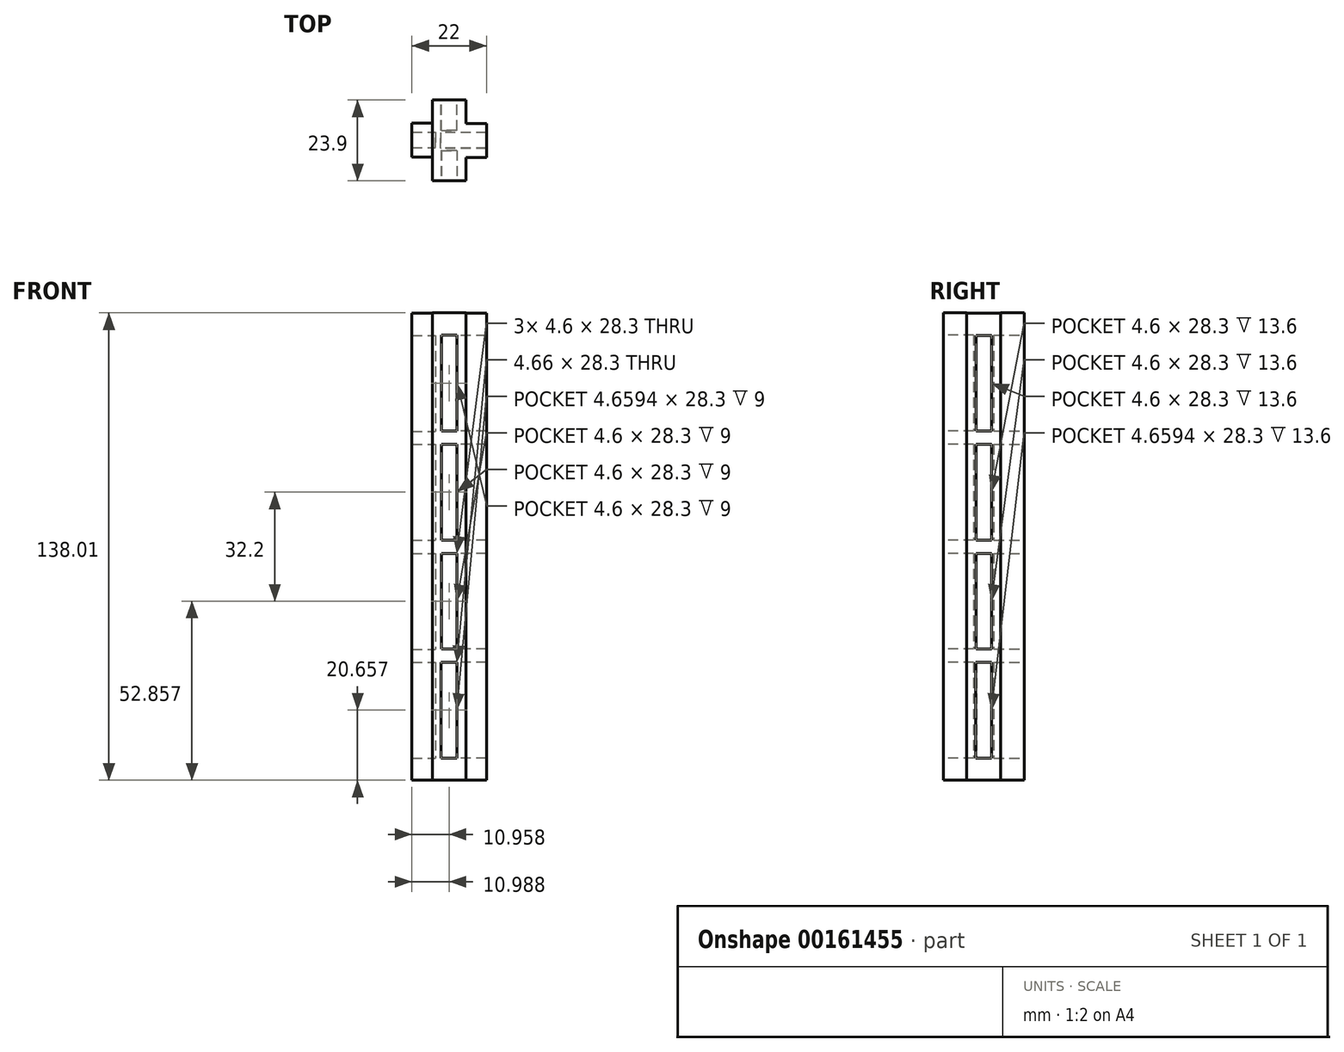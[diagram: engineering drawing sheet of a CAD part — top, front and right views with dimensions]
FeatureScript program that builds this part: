
annotation { "Feature Type Name" : "Feature", "Feature Type Description" : "" }
export const myFeature = defineFeature(function(context is Context, id is Id, definition is map)
    precondition{}
    {
        {
            var Q0;
            Q0=qCreatedBy(makeId("Front.planeOp"),FACE);
            var sketch = newSketch(context, id + "F0", { "sketchPlane" : qUnion([Q0])});
            skLineSegment(sketch, "E0.bottom", {"start": v(-30.25, 56.68) * mm, "end": v(-20.25, 56.68) * mm});
            skLineSegment(sketch, "E0.top", {"start": v(-30.25, -81.32) * mm, "end": v(-20.25, -81.32) * mm});
            skLineSegment(sketch, "E0.left", {"start": v(-30.25, 56.68) * mm, "end": v(-30.25, -81.32) * mm});
            skLineSegment(sketch, "E0.right", {"start": v(-20.25, 56.68) * mm, "end": v(-20.25, -81.32) * mm});
            skLineSegment(sketch, "E1.bottom", {"start": v(-27.56, 50.08) * mm, "end": v(-22.96, 50.08) * mm});
            skLineSegment(sketch, "E1.top", {"start": v(-27.56, 21.78) * mm, "end": v(-22.96, 21.78) * mm});
            skLineSegment(sketch, "E1.left", {"start": v(-27.56, 50.08) * mm, "end": v(-27.56, 21.78) * mm});
            skLineSegment(sketch, "E1.right", {"start": v(-22.96, 50.08) * mm, "end": v(-22.96, 21.78) * mm});
            skLineSegment(sketch, "E2", {"start": v(-26.53, 56.68) * mm, "end": v(-26.53, 50.08) * mm, "construction": true});
            skLineSegment(sketch, "E3", {"start": v(-27.56, 45.9) * mm, "end": v(-30.25, 45.9) * mm, "construction": true});
            skLineSegment(sketch, "E4", {"start": v(-22.96, 46.31) * mm, "end": v(-20.25, 46.31) * mm, "construction": true});
            skLineSegment(sketch, "E5", {"start": v(-25.26, 21.78) * mm, "end": v(-25.26, 17.88) * mm, "construction": true});
            skLineSegment(sketch, "E6", {"start": v(-27.56, 21.78) * mm, "end": v(-27.56, 17.88) * mm, "construction": true});
            skLineSegment(sketch, "E7", {"start": v(-22.96, 21.78) * mm, "end": v(-22.96, 17.88) * mm, "construction": true});
            skLineSegment(sketch, "E8.bottom", {"start": v(-27.56, 17.88) * mm, "end": v(-22.96, 17.88) * mm});
            skLineSegment(sketch, "E8.top", {"start": v(-27.56, -10.42) * mm, "end": v(-22.96, -10.42) * mm});
            skLineSegment(sketch, "E8.left", {"start": v(-27.56, 17.88) * mm, "end": v(-27.56, -10.42) * mm});
            skLineSegment(sketch, "E8.right", {"start": v(-22.96, 17.88) * mm, "end": v(-22.96, -10.42) * mm});
            skLineSegment(sketch, "E9", {"start": v(-22.96, -10.42) * mm, "end": v(-22.96, -14.32) * mm, "construction": true});
            skLineSegment(sketch, "E10", {"start": v(-27.56, -10.42) * mm, "end": v(-27.56, -14.32) * mm, "construction": true});
            skLineSegment(sketch, "E11.bottom", {"start": v(-27.56, -14.32) * mm, "end": v(-22.96, -14.32) * mm});
            skLineSegment(sketch, "E11.top", {"start": v(-27.56, -42.62) * mm, "end": v(-22.96, -42.62) * mm});
            skLineSegment(sketch, "E11.left", {"start": v(-27.56, -14.32) * mm, "end": v(-27.56, -42.62) * mm});
            skLineSegment(sketch, "E11.right", {"start": v(-22.96, -14.32) * mm, "end": v(-22.96, -42.62) * mm});
            skLineSegment(sketch, "E12", {"start": v(-27.56, -41.18) * mm, "end": v(-27.56, -42.62) * mm});
            skLineSegment(sketch, "E13", {"start": v(-22.96, -42.62) * mm, "end": v(-22.96, -46.52) * mm, "construction": true});
            skLineSegment(sketch, "E14.bottom", {"start": v(-22.96, -46.52) * mm, "end": v(-27.62, -46.52) * mm});
            skLineSegment(sketch, "E14.top", {"start": v(-22.96, -74.82) * mm, "end": v(-27.62, -74.82) * mm});
            skLineSegment(sketch, "E14.left", {"start": v(-22.96, -46.52) * mm, "end": v(-22.96, -74.82) * mm});
            skLineSegment(sketch, "E14.right", {"start": v(-27.62, -46.52) * mm, "end": v(-27.62, -74.82) * mm});
            skLineSegment(sketch, "E15", {"start": v(-22.96, -74.82) * mm, "end": v(-22.96, -81.32) * mm, "construction": true});
            skSolve(sketch);
        }
        {
            var Q0;
            Q0=makeQuery(id+"F0.imprint","IMPRINT",FACE,{"disambiguationData":[TD([[makeQuery(id+"F0.imprint","IMPRINT",EDGE,{"derivedFrom":sQuery(id+"F0.wireOp",EDGE,"E0.bottom")}),-1.0]])]});
            var Q1;
            Q1=makeQuery(id+"F0.imprint","IMPRINT",FACE,{"disambiguationData":[TD([[makeQuery(id+"F0.imprint","IMPRINT",EDGE,{"derivedFrom":sQuery(id+"F0.wireOp",EDGE,"E1.bottom")}),-1.0]])]});
            var Q2;
            Q2=makeQuery(id+"F0.imprint","IMPRINT",FACE,{"disambiguationData":[TD([[makeQuery(id+"F0.imprint","IMPRINT",EDGE,{"derivedFrom":sQuery(id+"F0.wireOp",EDGE,"E8.bottom")}),-1.0]])]});
            var Q3;
            Q3=makeQuery(id+"F0.imprint","IMPRINT",FACE,{"disambiguationData":[TD([[makeQuery(id+"F0.imprint","IMPRINT",EDGE,{"derivedFrom":sQuery(id+"F0.wireOp",EDGE,"E11.bottom")}),-1.0]])]});
            var Q4;
            Q4=makeQuery(id+"F0.imprint","IMPRINT",FACE,{"disambiguationData":[TD([[makeQuery(id+"F0.imprint","IMPRINT",EDGE,{"derivedFrom":sQuery(id+"F0.wireOp",EDGE,"E14.bottom")}),1.0]])]});
            extrude(context, id + "F1", {"entities" : qUnion([Q0, Q1, Q2, Q3, Q4]), "depth" : 11.95 * mm});
        }
        {
            var Q0;
            Q0=makeQuery(id+"F0.imprint","IMPRINT",FACE,{"disambiguationData":[TD([[makeQuery(id+"F0.imprint","IMPRINT",EDGE,{"derivedFrom":sQuery(id+"F0.wireOp",EDGE,"E1.bottom")}),-1.0]])]});
            var Q1;
            Q1=makeQuery(id+"F0.imprint","IMPRINT",FACE,{"disambiguationData":[TD([[makeQuery(id+"F0.imprint","IMPRINT",EDGE,{"derivedFrom":sQuery(id+"F0.wireOp",EDGE,"E8.bottom")}),-1.0]])]});
            var Q2;
            Q2=makeQuery(id+"F0.imprint","IMPRINT",FACE,{"disambiguationData":[TD([[makeQuery(id+"F0.imprint","IMPRINT",EDGE,{"derivedFrom":sQuery(id+"F0.wireOp",EDGE,"E11.bottom")}),-1.0]])]});
            var Q3;
            Q3=makeQuery(id+"F0.imprint","IMPRINT",FACE,{"disambiguationData":[TD([[makeQuery(id+"F0.imprint","IMPRINT",EDGE,{"derivedFrom":sQuery(id+"F0.wireOp",EDGE,"E14.bottom")}),1.0]])]});
            extrude(context, id + "F2", {"entities" : qUnion([Q0, Q1, Q2, Q3]), "operationType" : NewBodyOperationType.REMOVE, "depth" : 9 * mm});
        }
        {
            var Q0;
            Q0=makeQuery(id+"F1.opExtrude","SWEPT_BODY",BODY,{"disambiguationData":[OSD([sQuery(id+"F0.wireOp",EDGE,"E0.bottom"),sQuery(id+"F0.wireOp",EDGE,"E0.top"),sQuery(id+"F0.wireOp",EDGE,"E0.left"),sQuery(id+"F0.wireOp",EDGE,"E0.right")])]});
            var Q1;
            Q1=makeQuery(id+"F1.opExtrude","CAP_FACE",FACE,{"disambiguationData":[OSD([sQuery(id+"F0.wireOp",EDGE,"E0.bottom"),sQuery(id+"F0.wireOp",EDGE,"E0.top"),sQuery(id+"F0.wireOp",EDGE,"E0.left"),sQuery(id+"F0.wireOp",EDGE,"E0.right")])],"isStart":false});
            mirror(context, id + "F3", {"operationType" : NewBodyOperationType.ADD, "entities" : qUnion([Q0]), "mirrorPlane" : qUnion([Q1])});
        }
        {
            var Q0;
            {var subQ0=makeQuery(id+"F1.opExtrude","SWEPT_FACE",FACE,{"disambiguationData":[OSD([sQuery(id+"F0.wireOp",EDGE,"E0.right")])]});Q0=makeQuery(id+"F3.boolean.opBoolean","MERGE",FACE,{"derivedFrom":[subQ0,makeQuery(id+"F3.opPattern","COPY",FACE,{"derivedFrom":subQ0,"instanceName":"1"})]});}
            var sketch = newSketch(context, id + "F4", { "sketchPlane" : qUnion([Q0])});
            skLineSegment(sketch, "E16.bottom", {"start": v(-16.93, 56.67) * mm, "end": v(-6.93, 56.67) * mm});
            skLineSegment(sketch, "E16.top", {"start": v(-16.93, -81.33) * mm, "end": v(-6.93, -81.33) * mm});
            skLineSegment(sketch, "E16.left", {"start": v(-16.93, 56.67) * mm, "end": v(-16.93, -81.33) * mm});
            skLineSegment(sketch, "E16.right", {"start": v(-6.93, 56.67) * mm, "end": v(-6.93, -81.33) * mm});
            skLineSegment(sketch, "E17.bottom", {"start": v(-14.24, 50.07) * mm, "end": v(-9.64, 50.07) * mm});
            skLineSegment(sketch, "E17.top", {"start": v(-14.24, 21.77) * mm, "end": v(-9.64, 21.77) * mm});
            skLineSegment(sketch, "E17.left", {"start": v(-14.24, 50.07) * mm, "end": v(-14.24, 21.77) * mm});
            skLineSegment(sketch, "E17.right", {"start": v(-9.64, 50.07) * mm, "end": v(-9.64, 21.77) * mm});
            skLineSegment(sketch, "E18", {"start": v(-13.2, 56.67) * mm, "end": v(-13.2, 50.07) * mm, "construction": true});
            skLineSegment(sketch, "E19", {"start": v(-14.24, 45.9) * mm, "end": v(-16.93, 45.9) * mm, "construction": true});
            skLineSegment(sketch, "E20", {"start": v(-9.64, 46.3) * mm, "end": v(-6.93, 46.3) * mm, "construction": true});
            skLineSegment(sketch, "E21", {"start": v(-11.94, 21.77) * mm, "end": v(-11.94, 17.87) * mm, "construction": true});
            skLineSegment(sketch, "E22", {"start": v(-14.24, 21.77) * mm, "end": v(-14.24, 17.87) * mm, "construction": true});
            skLineSegment(sketch, "E23", {"start": v(-9.64, 21.77) * mm, "end": v(-9.64, 17.87) * mm, "construction": true});
            skLineSegment(sketch, "E24.bottom", {"start": v(-14.24, 17.87) * mm, "end": v(-9.64, 17.87) * mm});
            skLineSegment(sketch, "E24.top", {"start": v(-14.24, -10.43) * mm, "end": v(-9.64, -10.43) * mm});
            skLineSegment(sketch, "E24.left", {"start": v(-14.24, 17.87) * mm, "end": v(-14.24, -10.43) * mm});
            skLineSegment(sketch, "E24.right", {"start": v(-9.64, 17.87) * mm, "end": v(-9.64, -10.43) * mm});
            skLineSegment(sketch, "E25", {"start": v(-9.64, -10.43) * mm, "end": v(-9.64, -14.33) * mm, "construction": true});
            skLineSegment(sketch, "E26", {"start": v(-14.24, -10.43) * mm, "end": v(-14.24, -14.33) * mm, "construction": true});
            skLineSegment(sketch, "E27.bottom", {"start": v(-14.24, -14.33) * mm, "end": v(-9.64, -14.33) * mm});
            skLineSegment(sketch, "E27.top", {"start": v(-14.24, -42.63) * mm, "end": v(-9.64, -42.63) * mm});
            skLineSegment(sketch, "E27.left", {"start": v(-14.24, -14.33) * mm, "end": v(-14.24, -42.63) * mm});
            skLineSegment(sketch, "E27.right", {"start": v(-9.64, -14.33) * mm, "end": v(-9.64, -42.63) * mm});
            skLineSegment(sketch, "E28", {"start": v(-14.24, 18.57) * mm, "end": v(-14.24, -42.63) * mm});
            skLineSegment(sketch, "E29", {"start": v(-9.64, -42.63) * mm, "end": v(-9.64, -46.53) * mm, "construction": true});
            skLineSegment(sketch, "E30.bottom", {"start": v(-9.64, -46.53) * mm, "end": v(-14.3, -46.53) * mm});
            skLineSegment(sketch, "E30.top", {"start": v(-9.64, -74.83) * mm, "end": v(-14.3, -74.83) * mm});
            skLineSegment(sketch, "E30.left", {"start": v(-9.64, -46.53) * mm, "end": v(-9.64, -74.83) * mm});
            skLineSegment(sketch, "E30.right", {"start": v(-14.3, -46.53) * mm, "end": v(-14.3, -74.83) * mm});
            skLineSegment(sketch, "E31", {"start": v(-9.64, -74.83) * mm, "end": v(-9.64, -81.33) * mm, "construction": true});
            skSolve(sketch);
        }
        {
            var Q0;
            Q0=qSketchRegion(id+"F4",true);
            extrude(context, id + "F5", {"entities" : qUnion([Q0]), "operationType" : NewBodyOperationType.ADD, "depth" : 6 * mm});
        }
        {
            var Q0;
            {var subQ0=makeQuery(id+"F1.opExtrude","SWEPT_FACE",FACE,{"disambiguationData":[OSD([sQuery(id+"F0.wireOp",EDGE,"E0.right")])]});Q0=makeQuery(id+"F5.boolean.opBoolean","SPLIT",FACE,{"disambiguationData":[TD([makeQuery(id+"F5.opExtrude","SWEPT_FACE",FACE,{"disambiguationData":[OSD([sQuery(id+"F4.wireOp",EDGE,"E17.bottom")])]})])],"derivedFrom":makeQuery(id+"F3.boolean.opBoolean","MERGE",FACE,{"derivedFrom":[subQ0,makeQuery(id+"F3.opPattern","COPY",FACE,{"derivedFrom":subQ0,"instanceName":"1"})]})});}
            var Q1;
            {var subQ0=sQuery(id+"F4.wireOp",EDGE,"E24.bottom");var subQ3=makeQuery(id+"F1.opExtrude","SWEPT_FACE",FACE,{"disambiguationData":[OSD([sQuery(id+"F0.wireOp",EDGE,"E0.right")])]});Q1=makeQuery(id+"F5.boolean.opBoolean","SPLIT",FACE,{"disambiguationData":[TD([makeQuery(id+"F5.opExtrude","SWEPT_FACE",FACE,{"disambiguationData":[OSD([subQ0])]})])],"derivedFrom":makeQuery(id+"F3.boolean.opBoolean","MERGE",FACE,{"derivedFrom":[subQ3,makeQuery(id+"F3.opPattern","COPY",FACE,{"derivedFrom":subQ3,"instanceName":"1"})]})});}
            var Q2;
            {var subQ0=sQuery(id+"F4.wireOp",EDGE,"E27.bottom");var subQ3=makeQuery(id+"F1.opExtrude","SWEPT_FACE",FACE,{"disambiguationData":[OSD([sQuery(id+"F0.wireOp",EDGE,"E0.right")])]});Q2=makeQuery(id+"F5.boolean.opBoolean","SPLIT",FACE,{"disambiguationData":[TD([makeQuery(id+"F5.opExtrude","SWEPT_FACE",FACE,{"disambiguationData":[OSD([subQ0])]})])],"derivedFrom":makeQuery(id+"F3.boolean.opBoolean","MERGE",FACE,{"derivedFrom":[subQ3,makeQuery(id+"F3.opPattern","COPY",FACE,{"derivedFrom":subQ3,"instanceName":"1"})]})});}
            var Q3;
            {var subQ0=makeQuery(id+"F1.opExtrude","SWEPT_FACE",FACE,{"disambiguationData":[OSD([sQuery(id+"F0.wireOp",EDGE,"E0.right")])]});Q3=makeQuery(id+"F5.boolean.opBoolean","SPLIT",FACE,{"disambiguationData":[TD([makeQuery(id+"F5.opExtrude","SWEPT_FACE",FACE,{"disambiguationData":[OSD([sQuery(id+"F4.wireOp",EDGE,"E30.bottom")])]})])],"derivedFrom":makeQuery(id+"F3.boolean.opBoolean","MERGE",FACE,{"derivedFrom":[subQ0,makeQuery(id+"F3.opPattern","COPY",FACE,{"derivedFrom":subQ0,"instanceName":"1"})]})});}
            extrude(context, id + "F6", {"entities" : qUnion([Q0, Q1, Q2, Q3]), "operationType" : NewBodyOperationType.REMOVE, "oppositeDirection" : true, "depth" : 7.6 * mm});
        }
        {
            var Q0;
            {var subQ0=makeQuery(id+"F1.opExtrude","SWEPT_FACE",FACE,{"disambiguationData":[OSD([sQuery(id+"F0.wireOp",EDGE,"E0.left")])]});Q0=makeQuery(id+"F3.boolean.opBoolean","MERGE",FACE,{"derivedFrom":[subQ0,makeQuery(id+"F3.opPattern","COPY",FACE,{"derivedFrom":subQ0,"instanceName":"1"})]});}
            var sketch = newSketch(context, id + "F7", { "sketchPlane" : qUnion([Q0])});
            skLineSegment(sketch, "E32.bottom", {"start": v(6.83, 56.64) * mm, "end": v(16.83, 56.64) * mm});
            skLineSegment(sketch, "E32.top", {"start": v(6.83, -81.36) * mm, "end": v(16.83, -81.36) * mm});
            skLineSegment(sketch, "E32.left", {"start": v(6.83, 56.64) * mm, "end": v(6.83, -81.36) * mm});
            skLineSegment(sketch, "E32.right", {"start": v(16.83, 56.64) * mm, "end": v(16.83, -81.36) * mm});
            skLineSegment(sketch, "E33.bottom", {"start": v(9.52, 50.04) * mm, "end": v(14.12, 50.04) * mm});
            skLineSegment(sketch, "E33.top", {"start": v(9.52, 21.74) * mm, "end": v(14.12, 21.74) * mm});
            skLineSegment(sketch, "E33.left", {"start": v(9.52, 50.04) * mm, "end": v(9.52, 21.74) * mm});
            skLineSegment(sketch, "E33.right", {"start": v(14.12, 50.04) * mm, "end": v(14.12, 21.74) * mm});
            skLineSegment(sketch, "E34", {"start": v(10.56, 56.64) * mm, "end": v(10.56, 50.04) * mm, "construction": true});
            skLineSegment(sketch, "E35", {"start": v(9.52, 45.86) * mm, "end": v(6.83, 45.86) * mm, "construction": true});
            skLineSegment(sketch, "E36", {"start": v(14.12, 46.27) * mm, "end": v(16.83, 46.27) * mm, "construction": true});
            skLineSegment(sketch, "E37", {"start": v(11.82, 21.74) * mm, "end": v(11.82, 17.84) * mm, "construction": true});
            skLineSegment(sketch, "E38", {"start": v(9.52, 21.74) * mm, "end": v(9.52, 17.84) * mm, "construction": true});
            skLineSegment(sketch, "E39", {"start": v(14.12, 21.74) * mm, "end": v(14.12, 17.84) * mm, "construction": true});
            skLineSegment(sketch, "E40.bottom", {"start": v(9.52, 17.84) * mm, "end": v(14.12, 17.84) * mm});
            skLineSegment(sketch, "E40.top", {"start": v(9.52, -10.46) * mm, "end": v(14.12, -10.46) * mm});
            skLineSegment(sketch, "E40.left", {"start": v(9.52, 17.84) * mm, "end": v(9.52, -10.46) * mm});
            skLineSegment(sketch, "E40.right", {"start": v(14.12, 17.84) * mm, "end": v(14.12, -10.46) * mm});
            skLineSegment(sketch, "E41", {"start": v(14.12, -10.46) * mm, "end": v(14.12, -14.36) * mm, "construction": true});
            skLineSegment(sketch, "E42", {"start": v(9.52, -10.46) * mm, "end": v(9.52, -14.36) * mm, "construction": true});
            skLineSegment(sketch, "E43.bottom", {"start": v(9.52, -14.36) * mm, "end": v(14.12, -14.36) * mm});
            skLineSegment(sketch, "E43.top", {"start": v(9.52, -42.66) * mm, "end": v(14.12, -42.66) * mm});
            skLineSegment(sketch, "E43.left", {"start": v(9.52, -14.36) * mm, "end": v(9.52, -42.66) * mm});
            skLineSegment(sketch, "E43.right", {"start": v(14.12, -14.36) * mm, "end": v(14.12, -42.66) * mm});
            skLineSegment(sketch, "E44", {"start": v(9.52, -40.6) * mm, "end": v(9.52, -42.66) * mm});
            skLineSegment(sketch, "E45", {"start": v(14.12, -42.66) * mm, "end": v(14.12, -46.56) * mm, "construction": true});
            skLineSegment(sketch, "E46.bottom", {"start": v(14.12, -46.56) * mm, "end": v(9.46, -46.56) * mm});
            skLineSegment(sketch, "E46.top", {"start": v(14.12, -74.86) * mm, "end": v(9.46, -74.86) * mm});
            skLineSegment(sketch, "E46.left", {"start": v(14.12, -46.56) * mm, "end": v(14.12, -74.86) * mm});
            skLineSegment(sketch, "E46.right", {"start": v(9.46, -46.56) * mm, "end": v(9.46, -74.86) * mm});
            skLineSegment(sketch, "E47", {"start": v(14.12, -74.86) * mm, "end": v(14.12, -81.36) * mm, "construction": true});
            skSolve(sketch);
        }
        {
            var Q0;
            {var subQ0=sQuery(id+"F7.wireOp",EDGE,"E32.bottom");Q0=makeQuery(id+"F7.imprint","IMPRINT",FACE,{"disambiguationData":[TD([[makeQuery(id+"F7.imprint","IMPRINT",EDGE,{"derivedFrom":subQ0}),-1.0]])]});}
            var Q1;
            Q1=sQuery(id+"F7.wireOp",EDGE,"E32.bottom");
            var Q2;
            Q2=sQuery(id+"F7.wireOp",EDGE,"E32.top");
            var Q3;
            Q3=sQuery(id+"F7.wireOp",EDGE,"E32.left");
            var Q4;
            Q4=sQuery(id+"F7.wireOp",EDGE,"E32.right");
            var Q5;
            Q5=sQuery(id+"F7.wireOp",EDGE,"E33.bottom");
            var Q6;
            Q6=sQuery(id+"F7.wireOp",EDGE,"E33.top");
            var Q7;
            Q7=sQuery(id+"F7.wireOp",EDGE,"E33.left");
            var Q8;
            Q8=sQuery(id+"F7.wireOp",EDGE,"E33.right");
            var Q9;
            Q9=sQuery(id+"F7.wireOp",EDGE,"E40.bottom");
            var Q10;
            Q10=sQuery(id+"F7.wireOp",EDGE,"E40.top");
            var Q11;
            Q11=sQuery(id+"F7.wireOp",EDGE,"E40.left");
            var Q12;
            Q12=sQuery(id+"F7.wireOp",EDGE,"E40.right");
            var Q13;
            Q13=sQuery(id+"F7.wireOp",EDGE,"E43.bottom");
            var Q14;
            Q14=sQuery(id+"F7.wireOp",EDGE,"E43.top");
            var Q15;
            Q15=sQuery(id+"F7.wireOp",EDGE,"E43.left");
            var Q16;
            Q16=sQuery(id+"F7.wireOp",EDGE,"E43.right");
            var Q17;
            Q17=sQuery(id+"F7.wireOp",EDGE,"E44");
            var Q18;
            Q18=sQuery(id+"F7.wireOp",EDGE,"E46.bottom");
            var Q19;
            Q19=sQuery(id+"F7.wireOp",EDGE,"E46.top");
            var Q20;
            Q20=sQuery(id+"F7.wireOp",EDGE,"E46.left");
            var Q21;
            Q21=sQuery(id+"F7.wireOp",EDGE,"E46.right");
            extrude(context, id + "F8", {"entities" : qUnion([Q0]), "operationType" : NewBodyOperationType.ADD, "surfaceEntities" : qUnion([Q1, Q2, Q3, Q4, Q5, Q6, Q7, Q8, Q9, Q10, Q11, Q12, Q13, Q14, Q15, Q16, Q17, Q18, Q19, Q20, Q21]), "depth" : 6 * mm});
        }
        {
            var Q0;
            {var subQ0=makeQuery(id+"F1.opExtrude","SWEPT_FACE",FACE,{"disambiguationData":[OSD([sQuery(id+"F0.wireOp",EDGE,"E0.left")])]});Q0=makeQuery(id+"F8.boolean.opBoolean","SPLIT",FACE,{"disambiguationData":[TD([makeQuery(id+"F8.opExtrude","SWEPT_FACE",FACE,{"disambiguationData":[OSD([sQuery(id+"F7.wireOp",EDGE,"E33.bottom")])]})])],"derivedFrom":makeQuery(id+"F3.boolean.opBoolean","MERGE",FACE,{"derivedFrom":[subQ0,makeQuery(id+"F3.opPattern","COPY",FACE,{"derivedFrom":subQ0,"instanceName":"1"})]})});}
            var Q1;
            {var subQ0=makeQuery(id+"F1.opExtrude","SWEPT_FACE",FACE,{"disambiguationData":[OSD([sQuery(id+"F0.wireOp",EDGE,"E0.left")])]});Q1=makeQuery(id+"F8.boolean.opBoolean","SPLIT",FACE,{"disambiguationData":[TD([makeQuery(id+"F8.opExtrude","SWEPT_FACE",FACE,{"disambiguationData":[OSD([sQuery(id+"F7.wireOp",EDGE,"E40.bottom")])]})])],"derivedFrom":makeQuery(id+"F3.boolean.opBoolean","MERGE",FACE,{"derivedFrom":[subQ0,makeQuery(id+"F3.opPattern","COPY",FACE,{"derivedFrom":subQ0,"instanceName":"1"})]})});}
            var Q2;
            {var subQ0=makeQuery(id+"F1.opExtrude","SWEPT_FACE",FACE,{"disambiguationData":[OSD([sQuery(id+"F0.wireOp",EDGE,"E0.left")])]});Q2=makeQuery(id+"F8.boolean.opBoolean","SPLIT",FACE,{"disambiguationData":[TD([makeQuery(id+"F8.opExtrude","SWEPT_FACE",FACE,{"disambiguationData":[OSD([sQuery(id+"F7.wireOp",EDGE,"E46.bottom")])]})])],"derivedFrom":makeQuery(id+"F3.boolean.opBoolean","MERGE",FACE,{"derivedFrom":[subQ0,makeQuery(id+"F3.opPattern","COPY",FACE,{"derivedFrom":subQ0,"instanceName":"1"})]})});}
            var Q3;
            {var subQ0=makeQuery(id+"F1.opExtrude","SWEPT_FACE",FACE,{"disambiguationData":[OSD([sQuery(id+"F0.wireOp",EDGE,"E0.left")])]});Q3=makeQuery(id+"F8.boolean.opBoolean","SPLIT",FACE,{"disambiguationData":[TD([makeQuery(id+"F8.opExtrude","SWEPT_FACE",FACE,{"disambiguationData":[OSD([sQuery(id+"F7.wireOp",EDGE,"E43.bottom")])]})])],"derivedFrom":makeQuery(id+"F3.boolean.opBoolean","MERGE",FACE,{"derivedFrom":[subQ0,makeQuery(id+"F3.opPattern","COPY",FACE,{"derivedFrom":subQ0,"instanceName":"1"})]})});}
            extrude(context, id + "F9", {"entities" : qUnion([Q0, Q1, Q2, Q3]), "operationType" : NewBodyOperationType.REMOVE, "oppositeDirection" : true, "depth" : 1 * mm});
        }
    });
